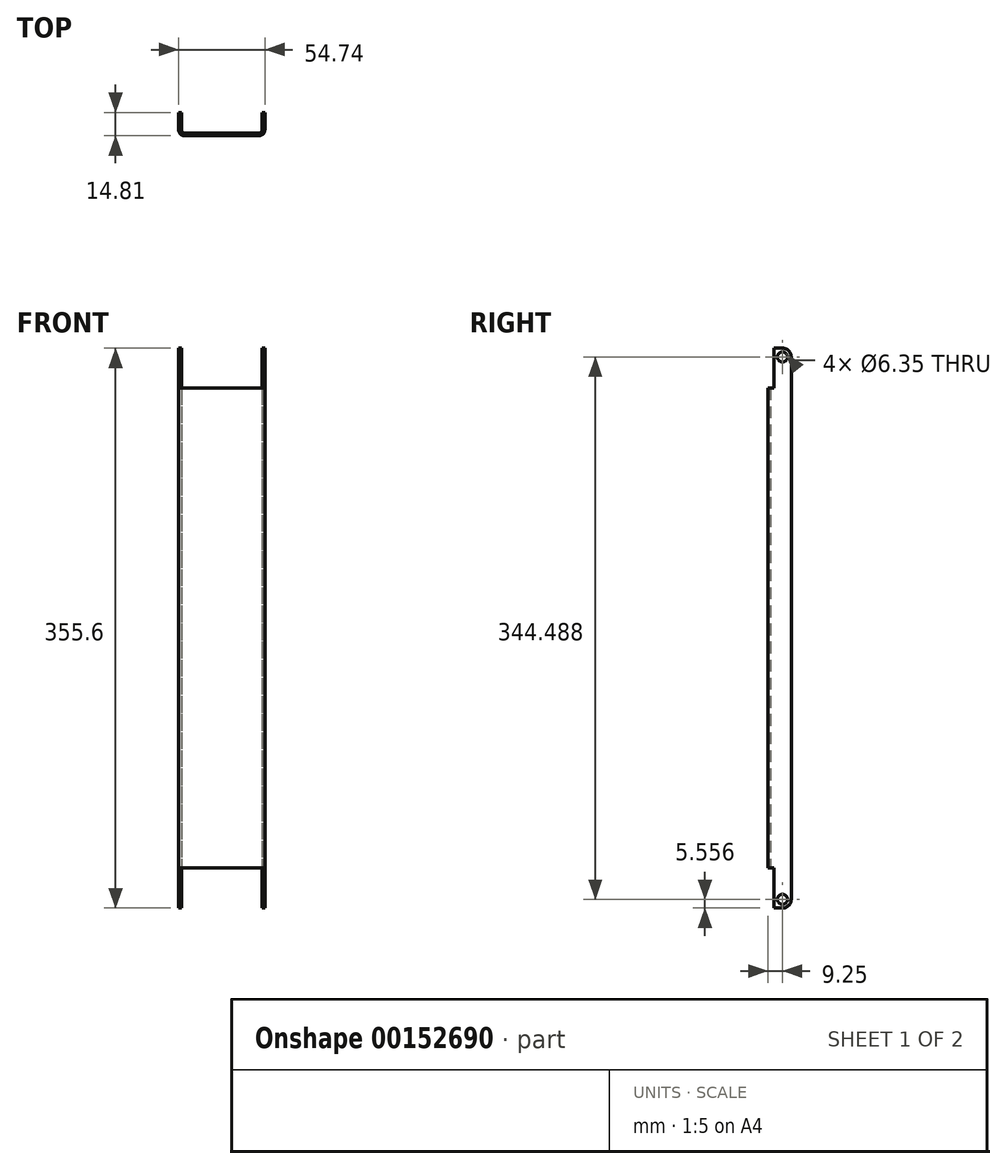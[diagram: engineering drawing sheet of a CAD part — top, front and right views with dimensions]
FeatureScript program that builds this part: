
annotation { "Feature Type Name" : "Feature", "Feature Type Description" : "" }
export const myFeature = defineFeature(function(context is Context, id is Id, definition is map)
    precondition{}
    {
        {
            var Q0;
            Q0=qCreatedBy(makeId("Top.planeOp"),FACE);
            var sketch = newSketch(context, id + "F0", { "sketchPlane" : qUnion([Q0])});
            skLineSegment(sketch, "E0.bottom", {"start": v(0, 0) * mm, "end": v(-51.32, 0) * mm});
            skLineSegment(sketch, "E0.top", {"start": v(1.7, -1.7) * mm, "end": v(-53.03, -1.7) * mm});
            skLineSegment(sketch, "E1.top", {"start": v(-51.32, 13.1) * mm, "end": v(-53.03, 13.1) * mm});
            skLineSegment(sketch, "E1.left", {"start": v(-51.32, 0) * mm, "end": v(-51.32, 13.1) * mm});
            skLineSegment(sketch, "E1.right", {"start": v(-53.03, -1.7) * mm, "end": v(-53.03, 13.1) * mm});
            skLineSegment(sketch, "E2.top", {"start": v(0, 13.1) * mm, "end": v(1.7, 13.1) * mm});
            skLineSegment(sketch, "E2.left", {"start": v(0, 0) * mm, "end": v(0, 13.1) * mm});
            skLineSegment(sketch, "E2.right", {"start": v(1.7, -1.7) * mm, "end": v(1.7, 13.1) * mm});
            skLineSegment(sketch, "E3", {"start": v(-25.66, 0) * mm, "end": v(-25.66, -1.7) * mm, "construction": true});
            skSolve(sketch);
        }
        {
            var Q0;
            Q0=qSketchRegion(id+"F0",true);
            extrude(context, id + "F1", {"entities" : qUnion([Q0]), "depth" : 304.8 * mm});
        }
        {
            var Q0;
            Q0=makeQuery(id+"F1.opExtrude","SWEPT_EDGE",EDGE,{"disambiguationData":[OSD([sQuery(id+"F0.wireOp",EDGE,"E0.top"),sQuery(id+"F0.wireOp",EDGE,"E2.right")])]});
            var Q1;
            Q1=makeQuery(id+"F1.opExtrude","SWEPT_EDGE",EDGE,{"disambiguationData":[OSD([sQuery(id+"F0.wireOp",EDGE,"E0.top"),sQuery(id+"F0.wireOp",EDGE,"E1.right")])]});
            var Q2;
            Q2=makeQuery(id+"FqNnmMD7oaRdpTN_1.opExtrude","CAP_EDGE",EDGE,{"disambiguationData":[OSD([sQuery(id+"FY5sMr6MULj5lJw_1.wireOp",EDGE,"W42EfhJi-fDm4-L9BW-folL-irsYfDskuzBk.top")])],"isStart":false});
            fillet(context, id + "F2", {"entities" : qUnion([Q0, Q1, Q2]), "radius" : 3.7 * mm, "tangentPropagation" : true, "allowEdgeOverflow" : false});
        }
        {
            var Q0;
            Q0=makeQuery(id+"F1.opExtrude","SWEPT_EDGE",EDGE,{"disambiguationData":[OSD([sQuery(id+"F0.wireOp",EDGE,"E0.bottom"),sQuery(id+"F0.wireOp",EDGE,"E2.left")])]});
            var Q1;
            Q1=makeQuery(id+"F1.opExtrude","SWEPT_EDGE",EDGE,{"disambiguationData":[OSD([sQuery(id+"F0.wireOp",EDGE,"E0.bottom"),sQuery(id+"F0.wireOp",EDGE,"E1.left")])]});
            fillet(context, id + "F3", {"entities" : qUnion([Q0, Q1]), "radius" : 1.98 * mm, "tangentPropagation" : true, "allowEdgeOverflow" : false});
        }
        {
            var Q0;
            Q0=makeQuery(id+"F1.opExtrude","SWEPT_FACE",FACE,{"disambiguationData":[OSD([sQuery(id+"F0.wireOp",EDGE,"E1.top")])]});
            var sketch = newSketch(context, id + "F4", { "sketchPlane" : qUnion([Q0])});
            skLineSegment(sketch, "E4.bottom", {"start": v(53.03, 0) * mm, "end": v(51.32, 0) * mm});
            skLineSegment(sketch, "E4.top", {"start": v(53.03, -25.4) * mm, "end": v(51.32, -25.4) * mm});
            skLineSegment(sketch, "E4.left", {"start": v(53.03, 0) * mm, "end": v(53.03, -25.4) * mm});
            skLineSegment(sketch, "E4.right", {"start": v(51.32, 0) * mm, "end": v(51.32, -25.4) * mm});
            skLineSegment(sketch, "E5.bottom", {"start": v(0, 0) * mm, "end": v(-1.7, 0) * mm});
            skLineSegment(sketch, "E5.top", {"start": v(0, -25.4) * mm, "end": v(-1.7, -25.4) * mm});
            skLineSegment(sketch, "E5.left", {"start": v(0, 0) * mm, "end": v(0, -25.4) * mm});
            skLineSegment(sketch, "E5.right", {"start": v(-1.7, 0) * mm, "end": v(-1.7, -25.4) * mm});
            skLineSegment(sketch, "E6.bottom", {"start": v(0, 304.8) * mm, "end": v(-1.7, 304.8) * mm});
            skLineSegment(sketch, "E6.top", {"start": v(0, 330.2) * mm, "end": v(-1.7, 330.2) * mm});
            skLineSegment(sketch, "E6.left", {"start": v(0, 304.8) * mm, "end": v(0, 330.2) * mm});
            skLineSegment(sketch, "E6.right", {"start": v(-1.7, 304.8) * mm, "end": v(-1.7, 330.2) * mm});
            skLineSegment(sketch, "E7.bottom", {"start": v(53.03, 304.8) * mm, "end": v(51.32, 304.8) * mm});
            skLineSegment(sketch, "E7.top", {"start": v(53.03, 330.2) * mm, "end": v(51.32, 330.2) * mm});
            skLineSegment(sketch, "E7.left", {"start": v(53.03, 304.8) * mm, "end": v(53.03, 330.2) * mm});
            skLineSegment(sketch, "E7.right", {"start": v(51.32, 304.8) * mm, "end": v(51.32, 330.2) * mm});
            skSolve(sketch);
        }
        {
            var Q0;
            Q0=makeQuery(id+"F1.opExtrude","SWEPT_FACE",FACE,{"disambiguationData":[OSD([sQuery(id+"F0.wireOp",EDGE,"E0.bottom")])]});
            cPlane(context, id + "F5", {"entities" : qUnion([Q0]), "cplaneType" : CPlaneType.OFFSET, "offset" : 1.98 * mm, "width" : 152.4 * mm, "height" : 152.4 * mm});
        }
        {
            var Q0;
            Q0=makeQuery(id+"F4.imprint","IMPRINT",FACE,{"disambiguationData":[TD([[makeQuery(id+"F4.imprint","IMPRINT",EDGE,{"derivedFrom":sQuery(id+"F4.wireOp",EDGE,"E7.bottom")}),1.0]])]});
            var Q1;
            Q1=makeQuery(id+"F4.imprint","IMPRINT",FACE,{"disambiguationData":[TD([[makeQuery(id+"F4.imprint","IMPRINT",EDGE,{"derivedFrom":sQuery(id+"F4.wireOp",EDGE,"E6.bottom")}),-1.0]])]});
            var Q2;
            Q2=makeQuery(id+"F4.imprint","IMPRINT",FACE,{"disambiguationData":[TD([[makeQuery(id+"F4.imprint","IMPRINT",EDGE,{"derivedFrom":sQuery(id+"F4.wireOp",EDGE,"E5.bottom")}),1.0]])]});
            var Q3;
            Q3=makeQuery(id+"F4.imprint","IMPRINT",FACE,{"disambiguationData":[TD([[makeQuery(id+"F4.imprint","IMPRINT",EDGE,{"derivedFrom":sQuery(id+"F4.wireOp",EDGE,"E4.bottom")}),-1.0]])]});
            var Q4;
            Q4=sQuery(id+"F4.wireOp",EDGE,"E4.left");
            var Q5;
            Q5=sQuery(id+"F4.wireOp",EDGE,"E7.left");
            var Q6;
            Q6=qCreatedBy(id+"F5.planeOp",FACE);
            extrude(context, id + "F6", {"entities" : qUnion([Q0, Q1, Q2, Q3]), "operationType" : NewBodyOperationType.ADD, "surfaceEntities" : qUnion([Q4, Q5]), "endBound" : BoundingType.UP_TO_SURFACE, "oppositeDirection" : true, "endBoundEntityFace" : qUnion([Q6]), "depth" : 25.4 * mm});
        }
        {
            var Q0;
            Q0=makeQuery(id+"F6.opExtrude","TWEAK_EDGE",EDGE,{"derivedFrom":[makeQuery(id+"F4.imprint","IMPRINT",EDGE,{"derivedFrom":sQuery(id+"F4.wireOp",EDGE,"E4.top")}),dummyQuery(id+"F5.planeOp",FACE)]});
            var Q1;
            Q1=makeQuery(id+"F6.opExtrude","CAP_EDGE",EDGE,{"disambiguationData":[OSD([sQuery(id+"F4.wireOp",EDGE,"E4.top")])],"isStart":true});
            var Q2;
            Q2=makeQuery(id+"F6.opExtrude","TWEAK_EDGE",EDGE,{"derivedFrom":[makeQuery(id+"F4.imprint","IMPRINT",EDGE,{"derivedFrom":sQuery(id+"F4.wireOp",EDGE,"E5.top")}),dummyQuery(id+"F5.planeOp",FACE)]});
            var Q3;
            Q3=makeQuery(id+"F6.opExtrude","CAP_EDGE",EDGE,{"disambiguationData":[OSD([sQuery(id+"F4.wireOp",EDGE,"E5.top")])],"isStart":true});
            var Q4;
            Q4=makeQuery(id+"F6.opExtrude","TWEAK_EDGE",EDGE,{"derivedFrom":[makeQuery(id+"F4.imprint","IMPRINT",EDGE,{"derivedFrom":sQuery(id+"F4.wireOp",EDGE,"E6.top")}),dummyQuery(id+"F5.planeOp",FACE)]});
            var Q5;
            Q5=makeQuery(id+"F6.opExtrude","CAP_EDGE",EDGE,{"disambiguationData":[OSD([sQuery(id+"F4.wireOp",EDGE,"E6.top")])],"isStart":true});
            var Q6;
            Q6=makeQuery(id+"F6.opExtrude","TWEAK_EDGE",EDGE,{"derivedFrom":[makeQuery(id+"F4.imprint","IMPRINT",EDGE,{"derivedFrom":sQuery(id+"F4.wireOp",EDGE,"E7.top")}),dummyQuery(id+"F5.planeOp",FACE)]});
            var Q7;
            Q7=makeQuery(id+"F6.opExtrude","CAP_EDGE",EDGE,{"disambiguationData":[OSD([sQuery(id+"F4.wireOp",EDGE,"E7.top")])],"isStart":true});
            fillet(context, id + "F7", {"entities" : qUnion([Q0, Q1, Q2, Q3, Q4, Q5, Q6, Q7]), "radius" : 5.56 * mm, "tangentPropagation" : true, "allowEdgeOverflow" : false});
        }
        {
            var Q0;
            Q0=makeQuery(id+"F6.boolean.opBoolean","MERGE",FACE,{"derivedFrom":[makeQuery(id+"F1.opExtrude","SWEPT_FACE",FACE,{"disambiguationData":[OSD([sQuery(id+"F0.wireOp",EDGE,"E2.right")])]}),makeQuery(id+"F6.opExtrude","SWEPT_FACE",FACE,{"disambiguationData":[OSD([sQuery(id+"F4.wireOp",EDGE,"E5.right")])]}),makeQuery(id+"F6.opExtrude","SWEPT_FACE",FACE,{"disambiguationData":[OSD([sQuery(id+"F4.wireOp",EDGE,"E6.right")])]})]});
            var sketch = newSketch(context, id + "F8", { "sketchPlane" : qUnion([Q0])});
            skCircle(sketch, "E8", {"center": v(7.54, -19.84) * mm, "radius": 3.18 * mm});
            skCircle(sketch, "E9", {"center": v(7.54, 324.64) * mm, "radius": 3.18 * mm});
            skSolve(sketch);
        }
        {
            var Q0;
            Q0 = qSketchRegion(id + "F8", true);
            var Q1;
            Q1=makeQuery(id+"F6.boolean.opBoolean","MERGE",FACE,{"derivedFrom":[makeQuery(id+"F1.opExtrude","SWEPT_FACE",FACE,{"disambiguationData":[OSD([sQuery(id+"F0.wireOp",EDGE,"E1.right")])]}),makeQuery(id+"F6.opExtrude","SWEPT_FACE",FACE,{"disambiguationData":[OSD([sQuery(id+"F4.wireOp",EDGE,"E4.left")])]}),makeQuery(id+"F6.opExtrude","SWEPT_FACE",FACE,{"disambiguationData":[OSD([sQuery(id+"F4.wireOp",EDGE,"E7.left")])]})]});
            extrude(context, id + "F9", {"entities" : qUnion([Q0]), "operationType" : NewBodyOperationType.REMOVE, "endBound" : BoundingType.UP_TO_SURFACE, "oppositeDirection" : true, "endBoundEntityFace" : qUnion([Q1]), "depth" : 25.4 * mm});
        }
    });
